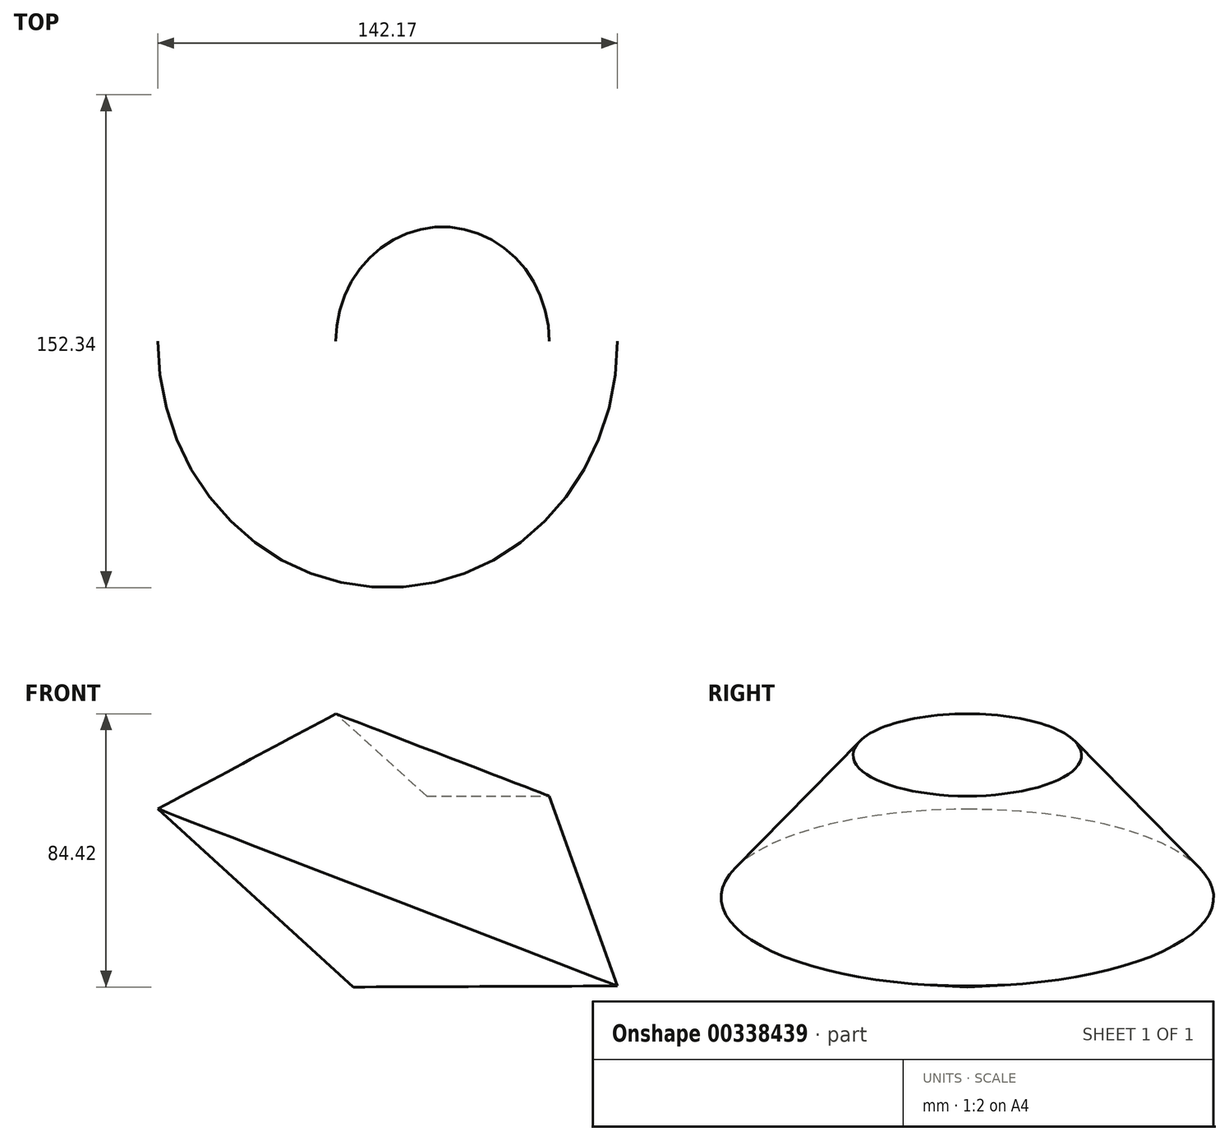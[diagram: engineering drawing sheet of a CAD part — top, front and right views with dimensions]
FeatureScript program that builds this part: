
annotation { "Feature Type Name" : "Feature", "Feature Type Description" : "" }
export const myFeature = defineFeature(function(context is Context, id is Id, definition is map)
    precondition{}
    {
        {
            var Q0;
            Q0=qCreatedBy(makeId("Front.planeOp"),FACE);
            var sketch = newSketch(context, id + "F0", { "sketchPlane" : qUnion([Q0])});
            skLineSegment(sketch, "E0", {"start": v(-32.82, -17.83) * mm, "end": v(-10.1, 41.19) * mm});
            skLineSegment(sketch, "E1", {"start": v(-10.1, 41.19) * mm, "end": v(27.77, 41.19) * mm});
            skLineSegment(sketch, "E2", {"start": v(27.77, 41.19) * mm, "end": v(48.92, -17.52) * mm});
            skLineSegment(sketch, "E3", {"start": v(48.92, -17.52) * mm, "end": v(-32.82, -17.83) * mm});
            skLineSegment(sketch, "E4", {"start": v(-32.82, -17.83) * mm, "end": v(-10.1, 41.19) * mm, "construction": true});
            skSolve(sketch);
        }
        {
            var Q0;
            Q0=makeQuery(id+"F0.imprint","IMPRINT",FACE,{"disambiguationData":[TD([[makeQuery(id+"F0.imprint","IMPRINT",EDGE,{"derivedFrom":sQuery(id+"F0.wireOp",EDGE,"E0")}),-1.0]])]});
            var Q1;
            Q1=sQuery(id+"F0.wireOp",EDGE,"E0");
            revolve(context, id + "F1", {"entities" : qUnion([Q0]), "axis" : qUnion([Q1]), "revolveType" : RevolveType.FULL});
        }
    });
